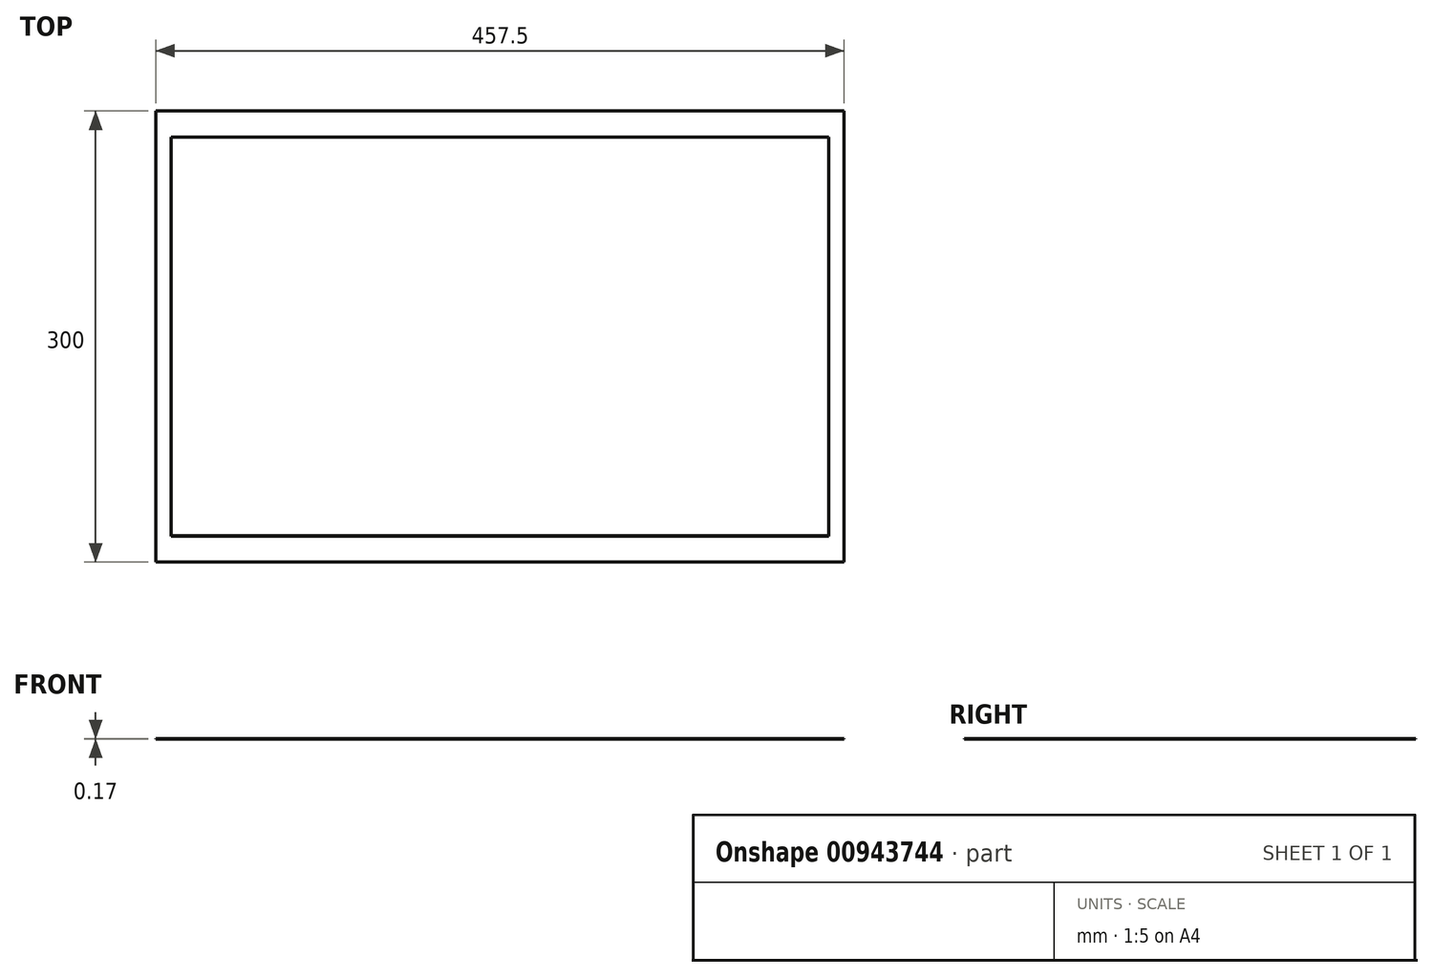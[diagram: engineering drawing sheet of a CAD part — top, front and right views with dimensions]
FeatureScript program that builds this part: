
annotation { "Feature Type Name" : "Feature", "Feature Type Description" : "" }
export const myFeature = defineFeature(function(context is Context, id is Id, definition is map)
    precondition{}
    {
        {
            var Q0;
            Q0=qCreatedBy(makeId("Top.planeOp"),FACE);
            var sketch = newSketch(context, id + "F0", { "sketchPlane" : qUnion([Q0])});
            skLineSegment(sketch, "E0.bottom", {"start": v(228.75, -150) * mm, "end": v(-228.75, -150) * mm});
            skLineSegment(sketch, "E0.top", {"start": v(228.75, 150) * mm, "end": v(-228.75, 150) * mm});
            skLineSegment(sketch, "E0.left", {"start": v(228.75, -150) * mm, "end": v(228.75, 150) * mm});
            skLineSegment(sketch, "E0.right", {"start": v(-228.75, -150) * mm, "end": v(-228.75, 150) * mm});
            skPoint(sketch, "E0.middle", {"position": v(0, 0) * mm});
            skSolve(sketch);
        }
        {
            var Q0;
            Q0 = qSketchRegion(id + "F0", true);
            extrude(context, id + "F1", {"entities" : qUnion([Q0]), "depth" : 0.17 * mm, "offsetDistance" : 25 * mm});
        }
        {
            var Q0;
            Q0=makeQuery(id+"F1.opExtrude","CAP_FACE",FACE,{"disambiguationData":[OSD([sQuery(id+"F0.wireOp",EDGE,"E0.bottom"),sQuery(id+"F0.wireOp",EDGE,"E0.top"),sQuery(id+"F0.wireOp",EDGE,"E0.left"),sQuery(id+"F0.wireOp",EDGE,"E0.right")])],"isStart":false});
            var sketch = newSketch(context, id + "F2", { "sketchPlane" : qUnion([Q0])});
            skLineSegment(sketch, "E1.bottom", {"start": v(218.5, -132.5) * mm, "end": v(-218.5, -132.5) * mm});
            skLineSegment(sketch, "E1.top", {"start": v(218.5, 132.5) * mm, "end": v(-218.5, 132.5) * mm});
            skLineSegment(sketch, "E1.left", {"start": v(218.5, -132.5) * mm, "end": v(218.5, 132.5) * mm});
            skLineSegment(sketch, "E1.right", {"start": v(-218.5, -132.5) * mm, "end": v(-218.5, 132.5) * mm});
            skPoint(sketch, "E1.middle", {"position": v(0, 0) * mm});
            skLineSegment(sketch, "E2.0", {"start": v(218.7, 132.7) * mm, "end": v(-218.7, 132.7) * mm});
            skLineSegment(sketch, "E2.1", {"start": v(218.7, -132.7) * mm, "end": v(218.7, 132.7) * mm});
            skLineSegment(sketch, "E2.2", {"start": v(218.7, -132.7) * mm, "end": v(-218.7, -132.7) * mm});
            skLineSegment(sketch, "E2.3", {"start": v(-218.7, -132.7) * mm, "end": v(-218.7, 132.7) * mm});
            skSolve(sketch);
        }
        {
            var Q0;
            Q0 = qSketchRegion(id + "F2", true);
            extrude(context, id + "F3", {"entities" : qUnion([Q0]), "operationType" : NewBodyOperationType.REMOVE, "oppositeDirection" : true, "depth" : 0.05 * mm, "offsetDistance" : 25 * mm});
        }
    });
